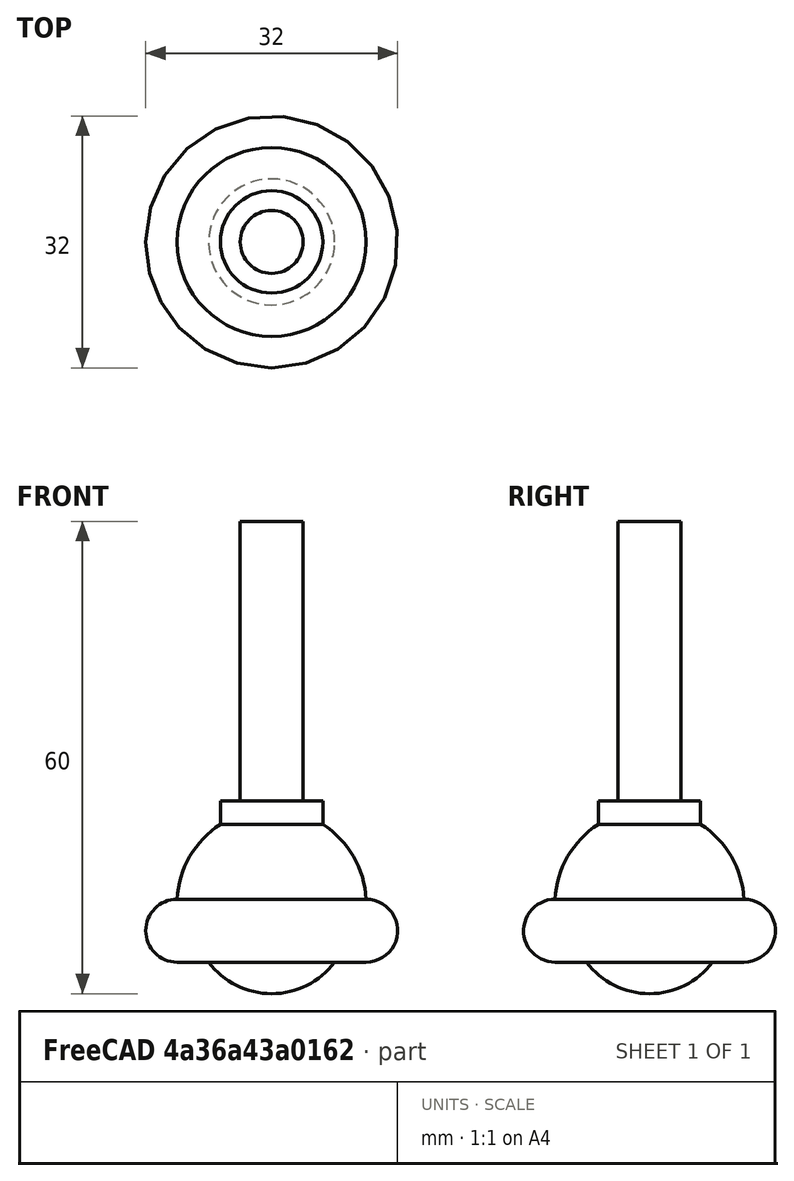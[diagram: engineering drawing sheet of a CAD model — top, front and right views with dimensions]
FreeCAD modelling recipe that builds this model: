
FCSTD DOCUMENT  (FreeCAD 0.15R4669 (Git))
Label: BR_billePorteuse
License: All rights reserved
LicenseURL: http://en.wikipedia.org/wiki/All_rights_reserved
objects: Sketcher::SketchObject×1, Part::Revolution×1
note: 2 computed .brp shape members not serialized (recipe doc carries the construction recipe); baked Part::Feature solids carry a one-line shape summary decoded from their .brp

FEATURE [Sketcher::SketchObject] Sketch
  Placement = pos=(0,0,0) rot=(-1,0,0;4.71239rad)
  sketch-geometry (9):
    g0: ArcOfCircle CenterX=0 CenterY=10 CenterZ=0 NormalX=0 NormalY=0 NormalZ=1 Radius=10 StartAngle=3.78509 EndAngle=4.71239
    g1: LineSegment StartX=-8 StartY=4 StartZ=0 EndX=-12 EndY=4 EndZ=0
    g2: ArcOfCircle CenterX=-12 CenterY=8 CenterZ=0 NormalX=0 NormalY=0 NormalZ=1 Radius=4 StartAngle=1.5708 EndAngle=4.71239
    g3: ArcOfCircle CenterX=0 CenterY=11.3947 CenterZ=0 NormalX=0 NormalY=0 NormalZ=1 Radius=12.0153 StartAngle=2.1424 EndAngle=3.0912
    g4: LineSegment StartX=-6.5 StartY=21.5 StartZ=0 EndX=-6.5 EndY=24.5 EndZ=0
    g5: LineSegment StartX=-6.5 StartY=24.5 StartZ=0 EndX=-4 EndY=24.5 EndZ=0
    g6: LineSegment StartX=-4 StartY=24.5 StartZ=0 EndX=-4 EndY=60 EndZ=0
    g7: LineSegment StartX=-4 StartY=60 StartZ=0 EndX=0 EndY=60 EndZ=0
    g8: LineSegment StartX=0 StartY=60 StartZ=0 EndX=0 EndY=0 EndZ=0
  constraints (29):
    c: Horizontal(g1)
    c: Coincident(g2,g1)
    c: Coincident(g3,g2)
    c: Coincident(g4,g5)
    c: Coincident(g5,g6)
    c: Vertical(g6)
    c: Coincident(g6,g7)
    c: Horizontal(g7)
    c: Coincident(g7,g8)
    c: Coincident(g8,g0)
    c: Vertical(g4)
    c: Horizontal(g5)
    c: Vertical(g8)
    c: Coincident(g0,g1)
    c: DistanceX(g-1,g0) = -8
    c: DistanceX(g7) = 4
    c: PointOnObject(g0,g-2)
    c: DistanceY(g8) = -60
    c: DistanceY(g6) = 35.5
    c: Tangent(g2,g1)
    c: Radius(g2) = 4
    c: Coincident(g4,g3)
    c: DistanceX(g-1,g1) = -12
    c: DistanceX(g5) = 2.5
    c: DistanceY(g4) = 3
    c: PointOnObject(g3,g-2)
    c: Angle(g2) = 3.14159
    c: DistanceY(g0,g6) = 56
    c: Coincident(g0,g-1)
FEATURE [Part::Revolution] Revolve  label="billePorteuse"
  Angle = 360
  Axis = (0,0,1)
  Base = (0,0,1)
  Solid = true
  Source = -> Sketch
